# Revit family: JAF 710-1600_Eng
name_source: partatom
category: Оборудование
units: mm (PartAtom-declared; Revit-internal decimal feet)

## family parameters
Всегда вертикально = Да
Классификация = Нет
На основе рабочей плоскости = Нет
Общий = Нет
При загрузке вырезать с полостями = Нет
Размер круглого соединителя = Использовать диаметр
Тип детали = Нормальный
Точка принадлежности помещению = Нет

## types (56) — shared parameters
00_20_Manufacturer = Vents
00_20_Name = Jet axial fan
Casing Material = Metal, painted, blue, matte RAL 5007
Frequency = 50 Гц
Load Classification = HVAC
Maintenance zone material = <По категории>
Number of Fase = 3
Thrust = 0.00 Н
Voltage = 400 В
t = 2 мм
Изготовитель = Vents
zero-valued in all types: Отметка по умолчанию

## per-type parameters (varying)
| type | A | Ay | Ayn | D_D | D_V | E | E1 | El | F | H | Height | L | L1 | Length | Maximum Air Flow | P | Power | R | Ry | Width | d |
| JAF‐Cl‐710‐2D/11‐U | 915 мм | 715 мм | 725 мм | 477 мм | 695 мм | 560 мм | 660 мм | 373 мм | 550 мм | 935 мм | 935 мм | 2800 мм | 1075 мм | 2800 мм | 43200.0 м³/ч | 90 мм | 11000 Вт | 458 мм | 358 мм | 915 мм | 20 мм |
| JAF‐Cl‐1600‐4D/90‐U‐R | 1815 мм | 1615 мм | 1625 мм | 1077 мм | 1595 мм | 1490 мм | 1590 мм | 823 мм | 970 мм | 1835 мм | 1835 мм | 5920 мм | 2410 мм | 5920 мм | 244800.0 м³/ч | 100 мм | 90000 Вт | 908 мм | 808 мм | 1815 мм | 30 мм |
| JAF‐Cl‐710‐2D/15‐U | 915 мм | 715 мм | 725 мм | 477 мм | 695 мм | 560 мм | 660 мм | 373 мм | 550 мм | 935 мм | 935 мм | 2800 мм | 1075 мм | 2800 мм | 47880.0 м³/ч | 90 мм | 15000 Вт | 458 мм | 358 мм | 915 мм | 20 мм |
| JAF‐Cl‐710‐2D/18.5‐U | 915 мм | 715 мм | 725 мм | 477 мм | 695 мм | 560 мм | 660 мм | 373 мм | 600 мм | 935 мм | 935 мм | 2850 мм | 1075 мм | 2850 мм | 50400.0 м³/ч | 90 мм | 18500 Вт | 458 мм | 358 мм | 915 мм | 20 мм |
| JAF‐Cl‐710‐2D/22‐U | 915 мм | 715 мм | 725 мм | 477 мм | 695 мм | 560 мм | 660 мм | 373 мм | 600 мм | 935 мм | 935 мм | 2850 мм | 1075 мм | 2850 мм | 54720.0 м³/ч | 90 мм | 22000 Вт | 458 мм | 358 мм | 915 мм | 20 мм |
| JAF‐Cl‐710‐2D/11‐U‐R | 915 мм | 715 мм | 725 мм | 477 мм | 695 мм | 560 мм | 660 мм | 373 мм | 550 мм | 935 мм | 935 мм | 2800 мм | 1075 мм | 2800 мм | 42840.0 м³/ч | 90 мм | 11000 Вт | 458 мм | 358 мм | 915 мм | 20 мм |
| JAF‐Cl‐710‐2D/15‐U‐R | 915 мм | 715 мм | 725 мм | 477 мм | 695 мм | 560 мм | 660 мм | 373 мм | 550 мм | 935 мм | 935 мм | 2800 мм | 1075 мм | 2800 мм | 43200.0 м³/ч | 90 мм | 15000 Вт | 458 мм | 358 мм | 915 мм | 20 мм |
| JAF‐Cl‐710‐2D/18.5‐U‐R | 915 мм | 715 мм | 725 мм | 477 мм | 695 мм | 560 мм | 660 мм | 373 мм | 600 мм | 935 мм | 935 мм | 2850 мм | 1075 мм | 2850 мм | 46440.0 м³/ч | 90 мм | 18500 Вт | 458 мм | 358 мм | 915 мм | 20 мм |
| JAF‐Cl‐710‐2D/22‐U‐R | 915 мм | 715 мм | 725 мм | 477 мм | 695 мм | 560 мм | 660 мм | 373 мм | 600 мм | 935 мм | 935 мм | 2850 мм | 1075 мм | 2850 мм | 49680.0 м³/ч | 90 мм | 22000 Вт | 458 мм | 358 мм | 915 мм | 20 мм |
| JAF‐Cl‐900‐4D/11‐U | 1135 мм | 935 мм | 945 мм | 623 мм | 915 мм | 730 мм | 830 мм | 483 мм | 550 мм | 1150 мм | 1150 мм | 3370 мм | 1360 мм | 3370 мм | 61560.0 м³/ч | 90 мм | 11000 Вт | 568 мм | 468 мм | 1135 мм | 20 мм |
| JAF‐Cl‐900‐4D/15‐U | 1135 мм | 935 мм | 945 мм | 623 мм | 915 мм | 730 мм | 830 мм | 483 мм | 600 мм | 1150 мм | 1150 мм | 3420 мм | 1360 мм | 3420 мм | 63360.0 м³/ч | 90 мм | 15000 Вт | 568 мм | 468 мм | 1135 мм | 20 мм |
| JAF‐Cl‐900‐4D/18.5‐U | 1135 мм | 935 мм | 945 мм | 623 мм | 915 мм | 730 мм | 830 мм | 483 мм | 600 мм | 1150 мм | 1150 мм | 3420 мм | 1360 мм | 3420 мм | 67320.0 м³/ч | 90 мм | 18500 Вт | 568 мм | 468 мм | 1135 мм | 20 мм |
| JAF‐Cl‐900‐4D/11‐U‐R | 1135 мм | 935 мм | 945 мм | 623 мм | 915 мм | 730 мм | 830 мм | 483 мм | 550 мм | 1150 мм | 1150 мм | 3370 мм | 1360 мм | 3370 мм | 52200.0 м³/ч | 90 мм | 11000 Вт | 568 мм | 468 мм | 1135 мм | 20 мм |
| JAF‐Cl‐900‐4D/15‐U‐R | 1135 мм | 935 мм | 945 мм | 623 мм | 915 мм | 730 мм | 830 мм | 483 мм | 600 мм | 1150 мм | 1150 мм | 3420 мм | 1360 мм | 3420 мм | 56520.0 м³/ч | 90 мм | 15000 Вт | 568 мм | 468 мм | 1135 мм | 20 мм |
| JAF‐Cl‐1000‐4D/15‐U | 1265 мм | 1065 мм | 1075 мм | 710 мм | 1045 мм | 895 мм | 995 мм | 548 мм | 575 мм | 1285 мм | 1285 мм | 3720 мм | 1510 мм | 3720 мм | 78840.0 м³/ч | 90 мм | 15000 Вт | 633 мм | 533 мм | 1265 мм | 20 мм |
| JAF‐Cl‐1000‐4D/18.5‐U | 1265 мм | 1065 мм | 1075 мм | 710 мм | 1045 мм | 895 мм | 995 мм | 548 мм | 575 мм | 1285 мм | 1285 мм | 3720 мм | 1510 мм | 3720 мм | 83880.0 м³/ч | 90 мм | 18500 Вт | 633 мм | 533 мм | 1265 мм | 20 мм |
| JAF‐Cl‐1000‐4D/22‐U | 1265 мм | 1065 мм | 1075 мм | 710 мм | 1045 мм | 895 мм | 995 мм | 548 мм | 725 мм | 1285 мм | 1285 мм | 3870 мм | 1510 мм | 3870 мм | 86400.0 м³/ч | 90 мм | 22000 Вт | 633 мм | 533 мм | 1265 мм | 20 мм |
| JAF‐Cl‐1000‐4D/30‐U | 1265 мм | 1065 мм | 1075 мм | 710 мм | 1045 мм | 895 мм | 995 мм | 548 мм | 725 мм | 1285 мм | 1285 мм | 3870 мм | 1510 мм | 3870 мм | 90720.0 м³/ч | 90 мм | 30000 Вт | 633 мм | 533 мм | 1265 мм | 20 мм |
| JAF‐Cl‐1000‐4D/15‐U‐R | 1265 мм | 1065 мм | 1075 мм | 710 мм | 1045 мм | 895 мм | 995 мм | 548 мм | 575 мм | 1285 мм | 1285 мм | 3720 мм | 1510 мм | 3720 мм | 70920.0 м³/ч | 90 мм | 15000 Вт | 633 мм | 533 мм | 1265 мм | 20 мм |
| JAF‐Cl‐1000‐4D/22‐U‐R | 1265 мм | 1065 мм | 1075 мм | 710 мм | 1045 мм | 895 мм | 995 мм | 548 мм | 725 мм | 1285 мм | 1285 мм | 3870 мм | 1510 мм | 3870 мм | 75240.0 м³/ч | 90 мм | 22000 Вт | 633 мм | 533 мм | 1265 мм | 20 мм |
| JAF‐Cl‐1000‐4D/30‐U‐R | 1265 мм | 1065 мм | 1075 мм | 710 мм | 1045 мм | 895 мм | 995 мм | 548 мм | 725 мм | 1285 мм | 1285 мм | 3870 мм | 1510 мм | 3870 мм | 80640.0 м³/ч | 90 мм | 30000 Вт | 633 мм | 533 мм | 1265 мм | 20 мм |
| JAF‐Cl‐1120‐4D/22‐U | 1315 мм | 1115 мм | 1125 мм | 743 мм | 1095 мм | 1020 мм | 1120 мм | 573 мм | 720 мм | 1335 мм | 1335 мм | 4230 мм | 1690 мм | 4230 мм | 99000.0 м³/ч | 90 мм | 22000 Вт | 658 мм | 558 мм | 1315 мм | 20 мм |
| JAF‐Cl‐1120‐4D/30‐U | 1315 мм | 1115 мм | 1125 мм | 743 мм | 1095 мм | 1020 мм | 1120 мм | 573 мм | 720 мм | 1335 мм | 1335 мм | 4230 мм | 1690 мм | 4230 мм | 108720.0 м³/ч | 90 мм | 30000 Вт | 658 мм | 558 мм | 1315 мм | 20 мм |
| JAF‐Cl‐1120‐4D/37‐U | 1315 мм | 1115 мм | 1125 мм | 743 мм | 1095 мм | 1020 мм | 1120 мм | 573 мм | 720 мм | 1335 мм | 1335 мм | 4230 мм | 1690 мм | 4230 мм | 121320.0 м³/ч | 90 мм | 37000 Вт | 658 мм | 558 мм | 1315 мм | 20 мм |
| JAF‐Cl‐1120‐4D/45‐U | 1315 мм | 1115 мм | 1125 мм | 743 мм | 1095 мм | 1020 мм | 1120 мм | 573 мм | 720 мм | 1335 мм | 1335 мм | 4230 мм | 1690 мм | 4230 мм | 125280.0 м³/ч | 90 мм | 45000 Вт | 658 мм | 558 мм | 1315 мм | 20 мм |
| JAF‐Cl‐1120‐4D/55‐U | 1315 мм | 1115 мм | 1125 мм | 743 мм | 1095 мм | 1020 мм | 1120 мм | 573 мм | 870 мм | 1335 мм | 1335 мм | 4380 мм | 1690 мм | 4380 мм | 128880.0 м³/ч | 90 мм | 55000 Вт | 658 мм | 558 мм | 1315 мм | 20 мм |
| JAF‐Cl‐1120‐4D/18.5‐U‐R | 1315 мм | 1115 мм | 1125 мм | 743 мм | 1095 мм | 1020 мм | 1120 мм | 573 мм | 570 мм | 1335 мм | 1335 мм | 4080 мм | 1690 мм | 4080 мм | 87480.0 м³/ч | 90 мм | 18500 Вт | 658 мм | 558 мм | 1315 мм | 20 мм |
| JAF‐Cl‐1120‐4D/22‐U‐R | 1315 мм | 1115 мм | 1125 мм | 743 мм | 1095 мм | 1020 мм | 1120 мм | 573 мм | 720 мм | 1335 мм | 1335 мм | 4230 мм | 1690 мм | 4230 мм | 93600.0 м³/ч | 90 мм | 22000 Вт | 658 мм | 558 мм | 1315 мм | 20 мм |
| JAF‐Cl‐1120‐4D/30‐U‐R | 1315 мм | 1115 мм | 1125 мм | 743 мм | 1095 мм | 1020 мм | 1120 мм | 573 мм | 720 мм | 1335 мм | 1335 мм | 4230 мм | 1690 мм | 4230 мм | 101880.0 м³/ч | 90 мм | 30000 Вт | 658 мм | 558 мм | 1315 мм | 20 мм |
| JAF‐Cl‐1120‐4D/37‐U‐R | 1315 мм | 1115 мм | 1125 мм | 743 мм | 1095 мм | 1020 мм | 1120 мм | 573 мм | 720 мм | 1335 мм | 1335 мм | 4230 мм | 1690 мм | 4230 мм | 108720.0 м³/ч | 90 мм | 37000 Вт | 658 мм | 558 мм | 1315 мм | 20 мм |
| JAF‐Cl‐1120‐4D/45‐U‐R | 1315 мм | 1115 мм | 1125 мм | 743 мм | 1095 мм | 1020 мм | 1120 мм | 573 мм | 720 мм | 1335 мм | 1335 мм | 4230 мм | 1690 мм | 4230 мм | 111960.0 м³/ч | 90 мм | 45000 Вт | 658 мм | 558 мм | 1315 мм | 20 мм |
| JAF‐Cl‐1250‐4D/37‐U | 1415 мм | 1215 мм | 1225 мм | 810 мм | 1195 мм | 1120 мм | 1220 мм | 623 мм | 720 мм | 1435 мм | 1435 мм | 4620 мм | 1890 мм | 4620 мм | 141120.0 м³/ч | 90 мм | 37000 Вт | 708 мм | 608 мм | 1415 мм | 30 мм |
| JAF‐Cl‐1250‐4D/45‐U | 1415 мм | 1215 мм | 1225 мм | 810 мм | 1195 мм | 1120 мм | 1220 мм | 623 мм | 720 мм | 1435 мм | 1435 мм | 4620 мм | 1890 мм | 4620 мм | 149760.0 м³/ч | 90 мм | 45000 Вт | 708 мм | 608 мм | 1415 мм | 30 мм |
| JAF‐Cl‐1250‐4D/55‐U | 1415 мм | 1215 мм | 1225 мм | 810 мм | 1195 мм | 1120 мм | 1220 мм | 623 мм | 870 мм | 1435 мм | 1435 мм | 4770 мм | 1890 мм | 4770 мм | 158760.0 м³/ч | 90 мм | 55000 Вт | 708 мм | 608 мм | 1415 мм | 30 мм |
| JAF‐Cl‐1250‐4D/75‐U | 1415 мм | 1215 мм | 1225 мм | 810 мм | 1195 мм | 1120 мм | 1220 мм | 623 мм | 870 мм | 1435 мм | 1435 мм | 4770 мм | 1890 мм | 4770 мм | 174600.0 м³/ч | 90 мм | 75000 Вт | 708 мм | 608 мм | 1415 мм | 30 мм |
| JAF‐Cl‐1250‐4D/37‐U‐R | 1415 мм | 1215 мм | 1225 мм | 810 мм | 1195 мм | 1120 мм | 1220 мм | 623 мм | 720 мм | 1435 мм | 1435 мм | 4620 мм | 1890 мм | 4620 мм | 128160.0 м³/ч | 90 мм | 37000 Вт | 708 мм | 608 мм | 1415 мм | 30 мм |
| JAF‐Cl‐1250‐4D/45‐U‐R | 1415 мм | 1215 мм | 1225 мм | 810 мм | 1195 мм | 1120 мм | 1220 мм | 623 мм | 720 мм | 1435 мм | 1435 мм | 4620 мм | 1890 мм | 4620 мм | 136800.0 м³/ч | 90 мм | 45000 Вт | 708 мм | 608 мм | 1415 мм | 30 мм |
| JAF‐Cl‐1250‐4D/55‐U‐R | 1415 мм | 1215 мм | 1225 мм | 810 мм | 1195 мм | 1120 мм | 1220 мм | 623 мм | 870 мм | 1435 мм | 1435 мм | 4770 мм | 1890 мм | 4770 мм | 146160.0 м³/ч | 90 мм | 55000 Вт | 708 мм | 608 мм | 1415 мм | 30 мм |
| JAF‐Cl‐1250‐4D/75‐U‐R | 1415 мм | 1215 мм | 1225 мм | 810 мм | 1195 мм | 1120 мм | 1220 мм | 623 мм | 870 мм | 1435 мм | 1435 мм | 4770 мм | 1890 мм | 4770 мм | 154440.0 м³/ч | 90 мм | 75000 Вт | 708 мм | 608 мм | 1415 мм | 30 мм |
| JAF‐Cl‐1400‐4D/30‐U | 1615 мм | 1415 мм | 1425 мм | 943 мм | 1395 мм | 1295 мм | 1395 мм | 723 мм | 720 мм | 1635 мм | 1635 мм | 5070 мм | 2110 мм | 5070 мм | 149040.0 м³/ч | 90 мм | 30000 Вт | 808 мм | 708 мм | 1615 мм | 30 мм |
| JAF‐Cl‐1400‐4D/37‐U | 1615 мм | 1415 мм | 1425 мм | 943 мм | 1395 мм | 1295 мм | 1395 мм | 723 мм | 720 мм | 1635 мм | 1635 мм | 5070 мм | 2110 мм | 5070 мм | 158400.0 м³/ч | 90 мм | 37000 Вт | 808 мм | 708 мм | 1615 мм | 30 мм |
| JAF‐Cl‐1400‐4D/45‐U | 1615 мм | 1415 мм | 1425 мм | 943 мм | 1395 мм | 1295 мм | 1395 мм | 723 мм | 720 мм | 1635 мм | 1635 мм | 5070 мм | 2110 мм | 5070 мм | 172800.0 м³/ч | 90 мм | 45000 Вт | 808 мм | 708 мм | 1615 мм | 30 мм |
| JAF‐Cl‐1400‐4D/55‐U | 1615 мм | 1415 мм | 1425 мм | 943 мм | 1395 мм | 1295 мм | 1395 мм | 723 мм | 870 мм | 1635 мм | 1635 мм | 5220 мм | 2110 мм | 5220 мм | 188640.0 м³/ч | 90 мм | 55000 Вт | 808 мм | 708 мм | 1615 мм | 30 мм |
| JAF‐Cl‐1400‐4D/75‐U | 1615 мм | 1415 мм | 1425 мм | 943 мм | 1395 мм | 1295 мм | 1395 мм | 723 мм | 870 мм | 1635 мм | 1635 мм | 5220 мм | 2110 мм | 5220 мм | 204840.0 м³/ч | 90 мм | 75000 Вт | 808 мм | 708 мм | 1615 мм | 30 мм |
| JAF‐Cl‐1400‐4D/30‐U‐R | 1615 мм | 1415 мм | 1425 мм | 943 мм | 1395 мм | 1295 мм | 1395 мм | 723 мм | 720 мм | 1635 мм | 1635 мм | 5070 мм | 2110 мм | 5070 мм | 143640.0 м³/ч | 90 мм | 30000 Вт | 808 мм | 708 мм | 1615 мм | 30 мм |
| JAF‐Cl‐1400‐4D/37‐U‐R | 1615 мм | 1415 мм | 1425 мм | 943 мм | 1395 мм | 1295 мм | 1395 мм | 723 мм | 720 мм | 1635 мм | 1635 мм | 5070 мм | 2110 мм | 5070 мм | 153000.0 м³/ч | 90 мм | 37000 Вт | 808 мм | 708 мм | 1615 мм | 30 мм |
| JAF‐Cl‐1400‐4D/45‐U‐R | 1615 мм | 1415 мм | 1425 мм | 943 мм | 1395 мм | 1295 мм | 1395 мм | 723 мм | 720 мм | 1635 мм | 1635 мм | 5070 мм | 2110 мм | 5070 мм | 164520.0 м³/ч | 90 мм | 45000 Вт | 808 мм | 708 мм | 1615 мм | 30 мм |
| JAF‐Cl‐1400‐4D/55‐U‐R | 1615 мм | 1415 мм | 1425 мм | 943 мм | 1395 мм | 1295 мм | 1395 мм | 723 мм | 870 мм | 1635 мм | 1635 мм | 5220 мм | 2110 мм | 5220 мм | 173160.0 м³/ч | 90 мм | 55000 Вт | 808 мм | 708 мм | 1615 мм | 30 мм |
| JAF‐Cl‐1400‐4D/75‐U‐R | 1615 мм | 1415 мм | 1425 мм | 943 мм | 1395 мм | 1295 мм | 1395 мм | 723 мм | 870 мм | 1635 мм | 1635 мм | 5220 мм | 2110 мм | 5220 мм | 189000.0 м³/ч | 90 мм | 75000 Вт | 808 мм | 708 мм | 1615 мм | 30 мм |
| JAF‐Cl‐1600‐4D/45‐U | 1815 мм | 1615 мм | 1625 мм | 1077 мм | 1595 мм | 1490 мм | 1590 мм | 823 мм | 720 мм | 1835 мм | 1835 мм | 5670 мм | 2410 мм | 5670 мм | 196920.0 м³/ч | 100 мм | 45000 Вт | 908 мм | 808 мм | 1815 мм | 30 мм |
| JAF‐Cl‐1600‐4D/55‐U | 1815 мм | 1615 мм | 1625 мм | 1077 мм | 1595 мм | 1490 мм | 1590 мм | 823 мм | 870 мм | 1835 мм | 1835 мм | 5820 мм | 2410 мм | 5820 мм | 219240.0 м³/ч | 100 мм | 55000 Вт | 908 мм | 808 мм | 1815 мм | 30 мм |
| JAF‐Cl‐1600‐4D/75‐U | 1815 мм | 1615 мм | 1625 мм | 1077 мм | 1595 мм | 1490 мм | 1590 мм | 823 мм | 870 мм | 1835 мм | 1835 мм | 5820 мм | 2410 мм | 5820 мм | 243720.0 м³/ч | 100 мм | 75000 Вт | 908 мм | 808 мм | 1815 мм | 30 мм |
| JAF‐Cl‐1600‐4D/90‐U | 1815 мм | 1615 мм | 1625 мм | 1077 мм | 1595 мм | 1490 мм | 1590 мм | 823 мм | 970 мм | 1835 мм | 1835 мм | 5920 мм | 2410 мм | 5920 мм | 259920.0 м³/ч | 100 мм | 90000 Вт | 908 мм | 808 мм | 1815 мм | 30 мм |
| JAF‐Cl‐1600‐4D/45‐U‐R | 1815 мм | 1615 мм | 1625 мм | 1077 мм | 1595 мм | 1490 мм | 1590 мм | 823 мм | 720 мм | 1835 мм | 1835 мм | 5670 мм | 2410 мм | 5670 мм | 189720.0 м³/ч | 100 мм | 45000 Вт | 908 мм | 808 мм | 1815 мм | 30 мм |
| JAF‐Cl‐1600‐4D/55‐U‐R | 1815 мм | 1615 мм | 1625 мм | 1077 мм | 1595 мм | 1490 мм | 1590 мм | 823 мм | 870 мм | 1835 мм | 1835 мм | 5820 мм | 2410 мм | 5820 мм | 203760.0 м³/ч | 100 мм | 55000 Вт | 908 мм | 808 мм | 1815 мм | 30 мм |
| JAF‐Cl‐1600‐4D/75‐U‐R | 1815 мм | 1615 мм | 1625 мм | 1077 мм | 1595 мм | 1490 мм | 1590 мм | 823 мм | 870 мм | 1835 мм | 1835 мм | 5820 мм | 2410 мм | 5820 мм | 230040.0 м³/ч | 100 мм | 75000 Вт | 908 мм | 808 мм | 1815 мм | 30 мм |

note: column(s) folded — value = type name in every type: 00_20_Type
